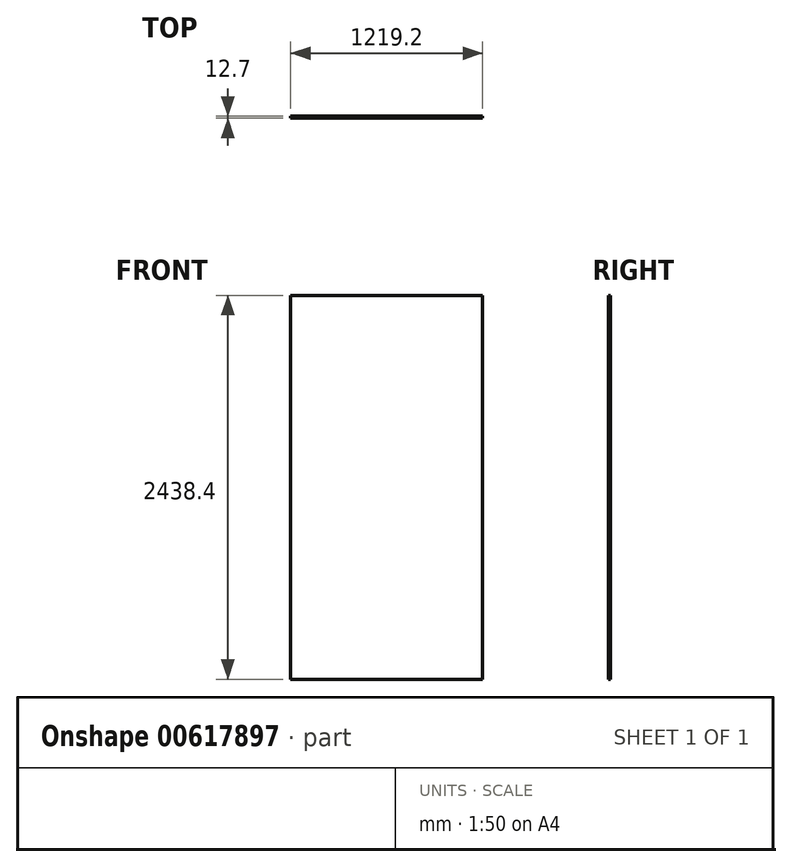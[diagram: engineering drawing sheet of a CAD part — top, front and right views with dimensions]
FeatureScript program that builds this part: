
annotation { "Feature Type Name" : "Feature", "Feature Type Description" : "" }
export const myFeature = defineFeature(function(context is Context, id is Id, definition is map)
    precondition{}
    {
        {
            var Q0;
            Q0=qCreatedBy(makeId("Front.planeOp"),FACE);
            var sketch = newSketch(context, id + "F0", { "sketchPlane" : qUnion([Q0])});
            skLineSegment(sketch, "E0.bottom", {"start": v(609.6, -1219.2) * mm, "end": v(-609.6, -1219.2) * mm});
            skLineSegment(sketch, "E0.top", {"start": v(609.6, 1219.2) * mm, "end": v(-609.6, 1219.2) * mm});
            skLineSegment(sketch, "E0.left", {"start": v(609.6, -1219.2) * mm, "end": v(609.6, 1219.2) * mm});
            skLineSegment(sketch, "E0.right", {"start": v(-609.6, -1219.2) * mm, "end": v(-609.6, 1219.2) * mm});
            skPoint(sketch, "E0.middle", {"position": v(0, 0) * mm});
            skSolve(sketch);
        }
        {
            var Q0;
            Q0=makeQuery(id+"F0.imprint","IMPRINT",FACE,{"disambiguationData":[TD([[makeQuery(id+"F0.imprint","IMPRINT",EDGE,{"derivedFrom":sQuery(id+"F0.wireOp",EDGE,"E0.bottom")}),-1.0]])]});
            extrude(context, id + "F1", {"entities" : qUnion([Q0]), "depth" : 12.7 * mm, "offsetDistance" : 25 * mm});
        }
    });
